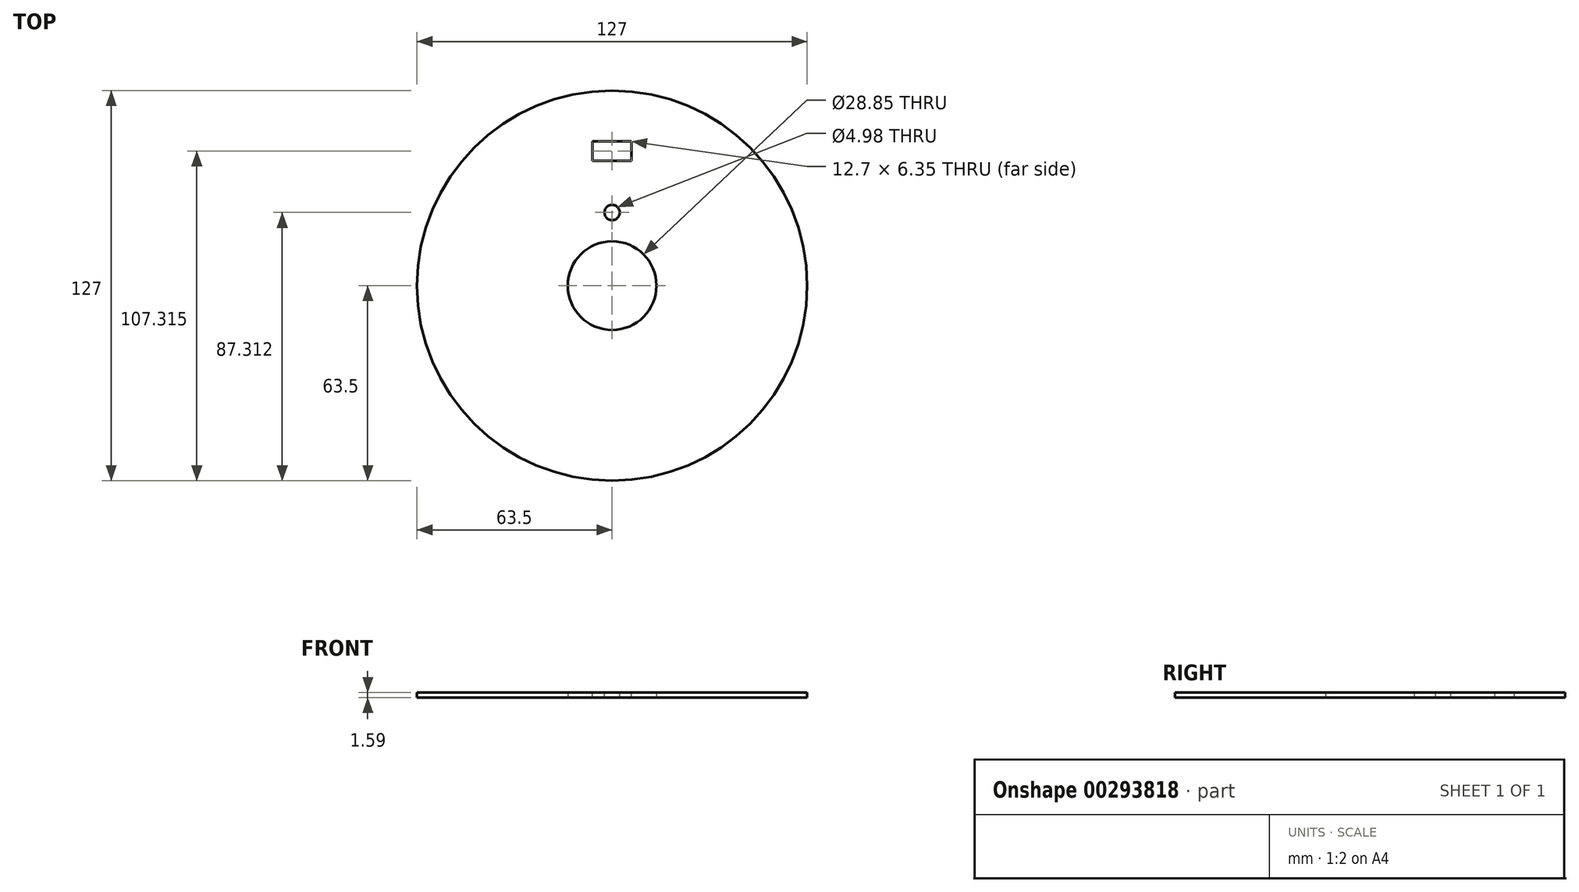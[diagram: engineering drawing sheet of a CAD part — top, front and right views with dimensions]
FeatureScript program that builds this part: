
annotation { "Feature Type Name" : "Feature", "Feature Type Description" : "" }
export const myFeature = defineFeature(function(context is Context, id is Id, definition is map)
    precondition{}
    {
        {
            var Q0;
            Q0=qCreatedBy(makeId("Top.planeOp"),FACE);
            var sketch = newSketch(context, id + "F0", { "sketchPlane" : qUnion([Q0])});
            skCircle(sketch, "E0", {"center": v(0, 0) * mm, "radius": 63.5 * mm});
            skCircle(sketch, "E1", {"center": v(0, 0) * mm, "radius": 14.43 * mm});
            skSolve(sketch);
        }
        {
            var Q0;
            Q0=makeQuery(id+"F0.imprint","IMPRINT",FACE,{"disambiguationData":[TD([[makeQuery(id+"F0.imprint","IMPRINT",EDGE,{"derivedFrom":sQuery(id+"F0.wireOp",EDGE,"E0")}),1.0]])]});
            var Q1;
            Q1=qSketchRegion(id+"F0",true);
            extrude(context, id + "F1", {"entities" : qUnion([Q0, Q1]), "depth" : 1.59 * mm});
        }
        {
            var Q0;
            Q0=makeQuery(id+"F1.opExtrude","CAP_FACE",FACE,{"disambiguationData":[OSD([sQuery(id+"F0.wireOp",EDGE,"E0"),sQuery(id+"F0.wireOp",EDGE,"E1")])],"isStart":false});
            var sketch = newSketch(context, id + "F2", { "sketchPlane" : qUnion([Q0])});
            skLineSegment(sketch, "E2.bottom", {"start": v(-6.35, 47) * mm, "end": v(6.35, 47) * mm});
            skLineSegment(sketch, "E2.top", {"start": v(-6.35, 40.64) * mm, "end": v(6.35, 40.64) * mm});
            skLineSegment(sketch, "E2.left", {"start": v(-6.35, 47) * mm, "end": v(-6.35, 40.64) * mm});
            skLineSegment(sketch, "E2.right", {"start": v(6.35, 47) * mm, "end": v(6.35, 40.64) * mm});
            skCircle(sketch, "E3", {"center": v(0, 0) * mm, "radius": 50.8 * mm, "construction": true});
            skPoint(sketch, "E4.middle", {"position": v(0, 40.38) * mm});
            skSolve(sketch);
        }
        {
            var Q0;
            Q0=qSketchRegion(id+"F2",true);
            extrude(context, id + "F3", {"entities" : qUnion([Q0]), "operationType" : NewBodyOperationType.REMOVE, "endBound" : BoundingType.THROUGH_ALL, "oppositeDirection" : true, "depth" : 25.4 * mm});
        }
        {
            var Q0;
            Q0=makeQuery(id+"F1.opExtrude","CAP_FACE",FACE,{"disambiguationData":[OSD([sQuery(id+"F0.wireOp",EDGE,"E0"),sQuery(id+"F0.wireOp",EDGE,"E1")])],"isStart":false});
            var sketch = newSketch(context, id + "F4", { "sketchPlane" : qUnion([Q0])});
            skCircle(sketch, "E5", {"center": v(0, 23.81) * mm, "radius": 2.49 * mm});
            skSolve(sketch);
        }
        {
            var Q0;
            Q0=qSketchRegion(id+"F4",true);
            extrude(context, id + "F5", {"entities" : qUnion([Q0]), "operationType" : NewBodyOperationType.REMOVE, "endBound" : BoundingType.THROUGH_ALL, "oppositeDirection" : true, "depth" : 25.4 * mm});
        }
    });
